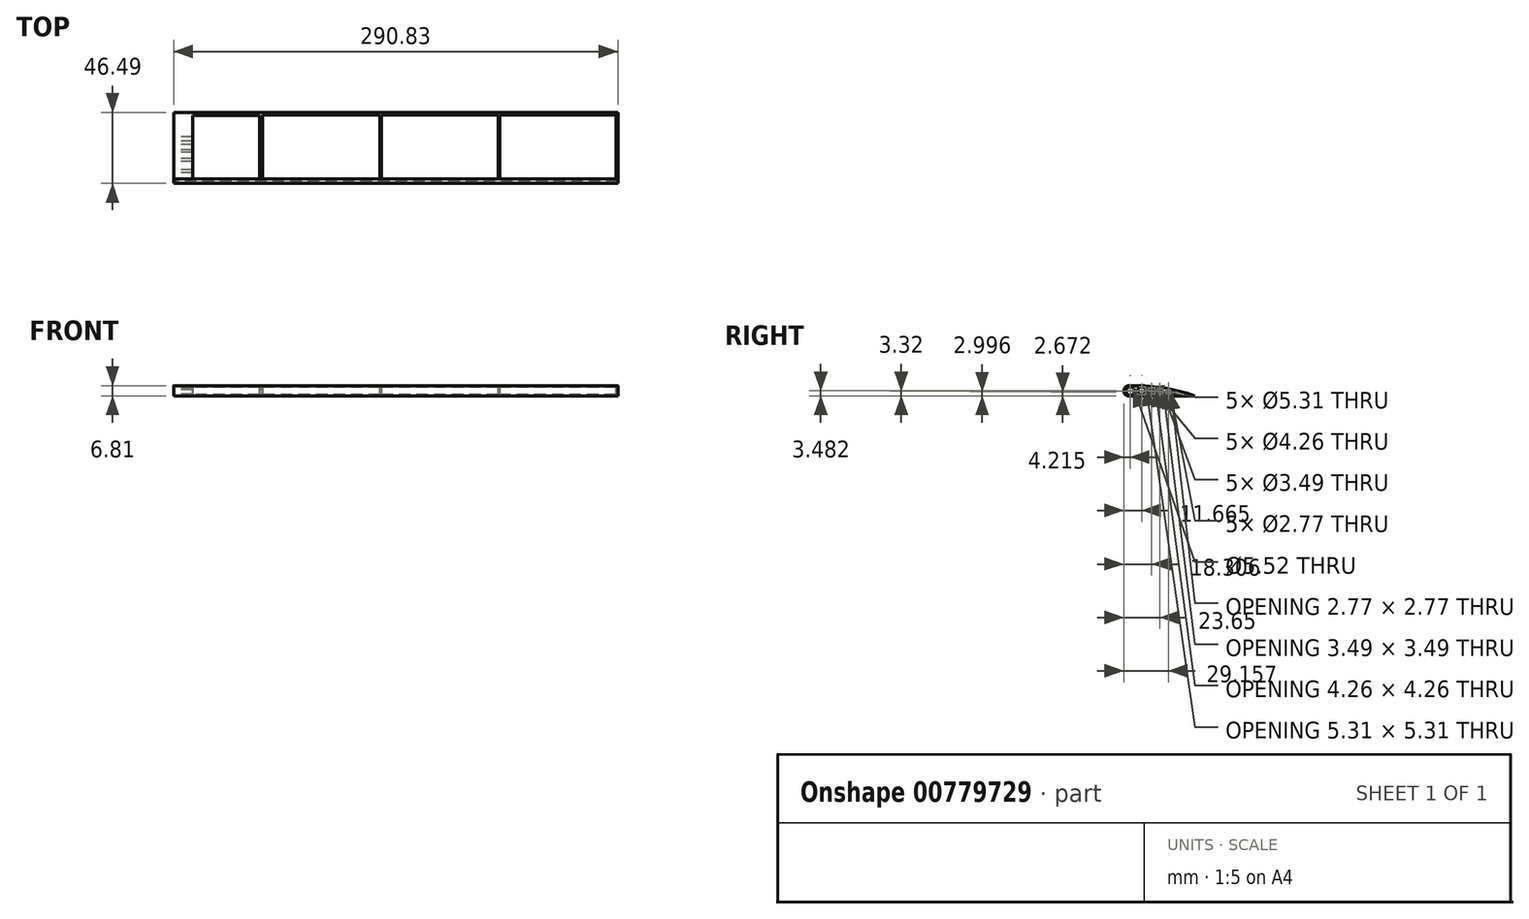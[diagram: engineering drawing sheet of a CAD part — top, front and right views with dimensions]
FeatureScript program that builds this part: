
annotation { "Feature Type Name" : "Feature", "Feature Type Description" : "" }
export const myFeature = defineFeature(function(context is Context, id is Id, definition is map)
    precondition{}
    {
        {
            var Q0;
            Q0=qCreatedBy(makeId("Right.planeOp"),FACE);
            var sketch = newSketch(context, id + "F0", { "sketchPlane" : qUnion([Q0])});
            skArc(sketch, "E0", {"start": v(0, 6.72) * mm, "mid": v(-3, 3.36) * mm, "end": v(0, 0) * mm});
            skArc(sketch, "E1", {"start": v(43.49, 0) * mm, "mid": v(22.07, 5.45) * mm, "end": v(0, 6.72) * mm});
            skLineSegment(sketch, "E2", {"start": v(0, 0) * mm, "end": v(43.49, 0) * mm});
            skSolve(sketch);
        }
        {
            var Q0;
            Q0 = qSketchRegion(id + "F0", true);
            extrude(context, id + "F1", {"entities" : qUnion([Q0]), "depth" : 290.83 * mm, "offsetDistance" : 25.4 * mm});
        }
        {
            var Q0;
            Q0=qCreatedBy(makeId("Right.planeOp"),FACE);
            var sketch = newSketch(context, id + "F2", { "sketchPlane" : qUnion([Q0])});
            skCircle(sketch, "E3", {"center": v(1.21, 3.32) * mm, "radius": 2.76 * mm});
            skSolve(sketch);
        }
        {
            var Q0;
            Q0 = qSketchRegion(id + "F2", true);
            extrude(context, id + "F3", {"entities" : qUnion([Q0]), "operationType" : NewBodyOperationType.REMOVE, "depth" : 488.95 * mm, "offsetDistance" : 25.4 * mm});
        }
        {
            var Q0;
            Q0=qCreatedBy(makeId("Right.planeOp"),FACE);
            var sketch = newSketch(context, id + "F4", { "sketchPlane" : qUnion([Q0])});
            skCircle(sketch, "E4", {"center": v(8.67, 3.48) * mm, "radius": 2.66 * mm});
            skSolve(sketch);
        }
        {
            var Q0;
            Q0 = qSketchRegion(id + "F4", true);
            extrude(context, id + "F5", {"entities" : qUnion([Q0]), "operationType" : NewBodyOperationType.REMOVE, "depth" : 389.9 * mm, "offsetDistance" : 25.4 * mm});
        }
        {
            var Q0;
            Q0=qCreatedBy(makeId("Right.planeOp"),FACE);
            var sketch = newSketch(context, id + "F6", { "sketchPlane" : qUnion([Q0])});
            skCircle(sketch, "E5", {"center": v(15.3, 3.32) * mm, "radius": 2.13 * mm});
            skSolve(sketch);
        }
        {
            var Q0;
            Q0 = qSketchRegion(id + "F6", true);
            extrude(context, id + "F7", {"entities" : qUnion([Q0]), "operationType" : NewBodyOperationType.REMOVE, "depth" : 366.27 * mm, "offsetDistance" : 25.4 * mm});
        }
        {
            var Q0;
            Q0=qCreatedBy(makeId("Right.planeOp"),FACE);
            var sketch = newSketch(context, id + "F8", { "sketchPlane" : qUnion([Q0])});
            skCircle(sketch, "E6", {"center": v(20.65, 3) * mm, "radius": 1.74 * mm});
            skSolve(sketch);
        }
        {
            var Q0;
            Q0 = qSketchRegion(id + "F8", true);
            extrude(context, id + "F9", {"entities" : qUnion([Q0]), "operationType" : NewBodyOperationType.REMOVE, "depth" : 536.7 * mm, "offsetDistance" : 25.4 * mm});
        }
        {
            var Q0;
            Q0=qCreatedBy(makeId("Right.planeOp"),FACE);
            var sketch = newSketch(context, id + "F10", { "sketchPlane" : qUnion([Q0])});
            skCircle(sketch, "E7", {"center": v(26.16, 2.67) * mm, "radius": 1.38 * mm});
            skSolve(sketch);
        }
        {
            var Q0;
            Q0 = qSketchRegion(id + "F10", true);
            extrude(context, id + "F11", {"entities" : qUnion([Q0]), "operationType" : NewBodyOperationType.REMOVE, "depth" : 596.65 * mm, "offsetDistance" : 25.4 * mm});
        }
        {
            var Q0;
            Q0=qCreatedBy(makeId("Top.planeOp"),FACE);
            cPlane(context, id + "F12", {"entities" : qUnion([Q0]), "cplaneType" : CPlaneType.OFFSET, "offset" : 41.66 * mm, "oppositeDirection" : true, "width" : 152.4 * mm, "height" : 152.4 * mm});
        }
        {
            var Q0;
            Q0=qCreatedBy(id+"F12.planeOp",FACE);
            var sketch = newSketch(context, id + "F13", { "sketchPlane" : qUnion([Q0])});
            skLineSegment(sketch, "E8.bottom", {"start": v(289.6, 0) * mm, "end": v(213.55, 0) * mm});
            skLineSegment(sketch, "E8.top", {"start": v(289.6, 42) * mm, "end": v(213.55, 42) * mm});
            skLineSegment(sketch, "E8.left", {"start": v(289.6, 0) * mm, "end": v(289.6, 42) * mm});
            skLineSegment(sketch, "E8.right", {"start": v(213.55, 0) * mm, "end": v(213.55, 42) * mm});
            skSolve(sketch);
        }
        {
            var Q0;
            Q0 = qSketchRegion(id + "F13", true);
            extrude(context, id + "F14", {"entities" : qUnion([Q0]), "operationType" : NewBodyOperationType.REMOVE, "depth" : 226.06 * mm, "offsetDistance" : 25.4 * mm});
        }
        {
            var Q0;
            Q0=qCreatedBy(id+"F12.planeOp",FACE);
            var sketch = newSketch(context, id + "F15", { "sketchPlane" : qUnion([Q0])});
            skLineSegment(sketch, "E9.bottom", {"start": v(212.52, 0) * mm, "end": v(135.96, 0) * mm});
            skLineSegment(sketch, "E9.top", {"start": v(212.52, 42) * mm, "end": v(135.96, 42) * mm});
            skLineSegment(sketch, "E9.left", {"start": v(212.52, 0) * mm, "end": v(212.52, 42) * mm});
            skLineSegment(sketch, "E9.right", {"start": v(135.96, 0) * mm, "end": v(135.96, 42) * mm});
            skSolve(sketch);
        }
        {
            var Q0;
            Q0 = qSketchRegion(id + "F15", true);
            extrude(context, id + "F16", {"entities" : qUnion([Q0]), "operationType" : NewBodyOperationType.REMOVE, "depth" : 224.03 * mm, "offsetDistance" : 25.4 * mm});
        }
        {
            var Q0;
            Q0=qCreatedBy(id+"F12.planeOp",FACE);
            var sketch = newSketch(context, id + "F17", { "sketchPlane" : qUnion([Q0])});
            skLineSegment(sketch, "E10.bottom", {"start": v(135.2, 0) * mm, "end": v(58.11, 0) * mm});
            skLineSegment(sketch, "E10.top", {"start": v(135.2, 41.75) * mm, "end": v(58.11, 41.75) * mm});
            skLineSegment(sketch, "E10.left", {"start": v(135.2, 0) * mm, "end": v(135.2, 41.75) * mm});
            skLineSegment(sketch, "E10.right", {"start": v(58.11, 0) * mm, "end": v(58.11, 41.75) * mm});
            skSolve(sketch);
        }
        {
            var Q0;
            Q0 = qSketchRegion(id + "F17", true);
            extrude(context, id + "F18", {"entities" : qUnion([Q0]), "operationType" : NewBodyOperationType.REMOVE, "depth" : 220.98 * mm, "offsetDistance" : 25.4 * mm});
        }
        {
            var Q0;
            Q0=qCreatedBy(id+"F12.planeOp",FACE);
            var sketch = newSketch(context, id + "F19", { "sketchPlane" : qUnion([Q0])});
            skLineSegment(sketch, "E11.bottom", {"start": v(56.32, 0) * mm, "end": v(12.38, 0) * mm});
            skLineSegment(sketch, "E11.top", {"start": v(56.32, 41.5) * mm, "end": v(12.38, 41.5) * mm});
            skLineSegment(sketch, "E11.left", {"start": v(56.32, 0) * mm, "end": v(56.32, 41.5) * mm});
            skLineSegment(sketch, "E11.right", {"start": v(12.38, 0) * mm, "end": v(12.38, 41.5) * mm});
            skSolve(sketch);
        }
        {
            var Q0;
            Q0 = qSketchRegion(id + "F19", true);
            extrude(context, id + "F20", {"entities" : qUnion([Q0]), "operationType" : NewBodyOperationType.REMOVE, "depth" : 92.7 * mm, "offsetDistance" : 25.4 * mm});
        }
        {
            var Q0;
            Q0=qCreatedBy(makeId("Right.planeOp"),FACE);
            cPlane(context, id + "F21", {"entities" : qUnion([Q0]), "cplaneType" : CPlaneType.OFFSET, "offset" : 431.04 * mm, "width" : 152.4 * mm, "height" : 152.4 * mm});
        }
    });
